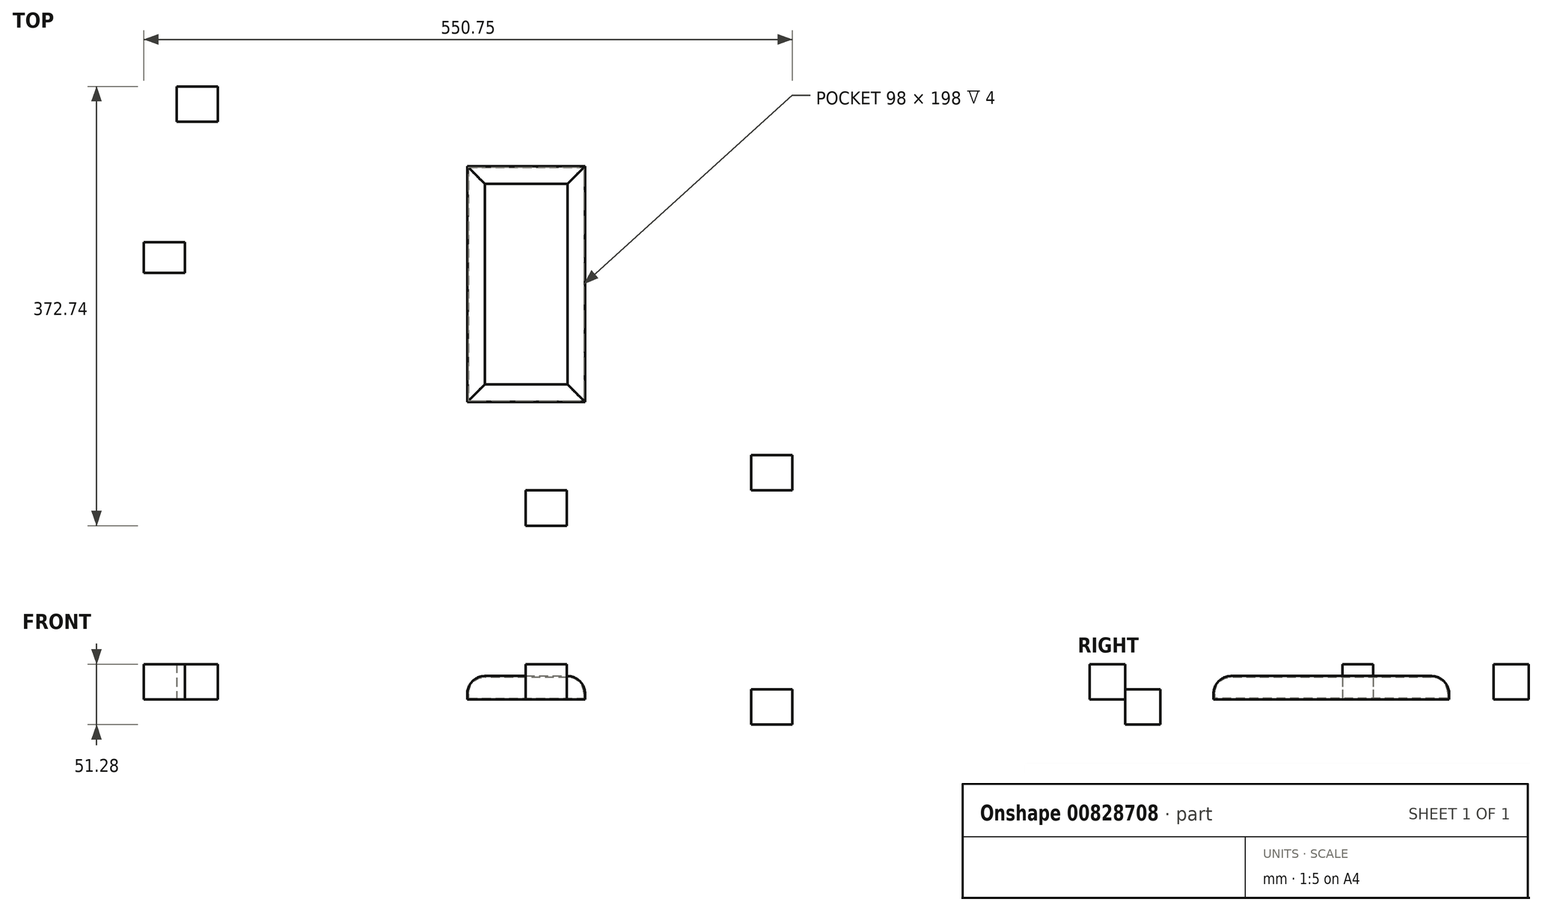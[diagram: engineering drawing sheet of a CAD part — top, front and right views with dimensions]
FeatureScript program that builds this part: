
annotation { "Feature Type Name" : "Feature", "Feature Type Description" : "" }
export const myFeature = defineFeature(function(context is Context, id is Id, definition is map)
    precondition{}
    {
        {
            var Q0;
            Q0=qCreatedBy(makeId("Top.planeOp"),FACE);
            var sketch = newSketch(context, id + "F0", { "sketchPlane" : qUnion([Q0])});
            skLineSegment(sketch, "E0.bottom", {"start": v(-289.22, 3.67) * mm, "end": v(-189.22, 3.67) * mm});
            skLineSegment(sketch, "E0.top", {"start": v(-289.22, -196.33) * mm, "end": v(-189.22, -196.33) * mm});
            skLineSegment(sketch, "E0.left", {"start": v(-289.22, 3.67) * mm, "end": v(-289.22, -196.33) * mm});
            skLineSegment(sketch, "E0.right", {"start": v(-189.22, 3.67) * mm, "end": v(-189.22, -196.33) * mm});
            skPoint(sketch, "E0.middle", {"position": v(-239.22, -96.33) * mm});
            skSolve(sketch);
        }
        {
            var Q0;
            Q0=makeQuery(id+"F0.imprint","IMPRINT",FACE,{"disambiguationData":[TD([[makeQuery(id+"F0.imprint","IMPRINT",EDGE,{"derivedFrom":sQuery(id+"F0.wireOp",EDGE,"E0.bottom")}),-1.0]])]});
            extrude(context, id + "F1", {"entities" : qUnion([Q0]), "depth" : 20 * mm, "offsetDistance" : 25 * mm});
        }
        {
            var Q0;
            Q0=makeQuery(id+"F1.opExtrude","CAP_EDGE",EDGE,{"disambiguationData":[OSD([sQuery(id+"F0.wireOp",EDGE,"E0.right")])],"isStart":false});
            var Q1;
            Q1=makeQuery(id+"F1.opExtrude","CAP_EDGE",EDGE,{"disambiguationData":[OSD([sQuery(id+"F0.wireOp",EDGE,"E0.top")])],"isStart":false});
            var Q2;
            Q2=makeQuery(id+"F1.opExtrude","CAP_EDGE",EDGE,{"disambiguationData":[OSD([sQuery(id+"F0.wireOp",EDGE,"E0.bottom")])],"isStart":false});
            var Q3;
            Q3=makeQuery(id+"F1.opExtrude","CAP_EDGE",EDGE,{"disambiguationData":[OSD([sQuery(id+"F0.wireOp",EDGE,"E0.left")])],"isStart":false});
            fillet(context, id + "F2", {"entities" : qUnion([Q0, Q1, Q2, Q3]), "radius" : 15 * mm, "tangentPropagation" : true, "allowEdgeOverflow" : false});
        }
        {
            var Q0;
            Q0=makeQuery(id+"F1.opExtrude","CAP_FACE",FACE,{"disambiguationData":[OSD([sQuery(id+"F0.wireOp",EDGE,"E0.bottom"),sQuery(id+"F0.wireOp",EDGE,"E0.top"),sQuery(id+"F0.wireOp",EDGE,"E0.left"),sQuery(id+"F0.wireOp",EDGE,"E0.right")])],"isStart":false});
            shell(context, id + "F3", {"entities" : qUnion([Q0]), "thickness" : 1 * mm});
        }
        {
            var Q0;
            Q0=qCreatedBy(makeId("Top.planeOp"),FACE);
            var sketch = newSketch(context, id + "F4", { "sketchPlane" : qUnion([Q0])});
            skLineSegment(sketch, "E1.bottom", {"start": v(-239.75, -271.36) * mm, "end": v(-204.75, -271.36) * mm});
            skLineSegment(sketch, "E1.top", {"start": v(-239.75, -301.36) * mm, "end": v(-204.75, -301.36) * mm});
            skLineSegment(sketch, "E1.left", {"start": v(-239.75, -271.36) * mm, "end": v(-239.75, -301.36) * mm});
            skLineSegment(sketch, "E1.right", {"start": v(-204.75, -271.36) * mm, "end": v(-204.75, -301.36) * mm});
            skSolve(sketch);
        }
        {
            var Q0;
            Q0 = qSketchRegion(id + "F4", true);
            extrude(context, id + "F5", {"entities" : qUnion([Q0]), "depth" : 30 * mm, "offsetDistance" : 25 * mm});
        }
        {
            var Q0;
            Q0=makeQuery(id+"F5.opExtrude","SWEPT_FACE",FACE,{"disambiguationData":[OSD([sQuery(id+"F4.wireOp",EDGE,"E1.bottom")])]});
            var sketch = newSketch(context, id + "F6", { "sketchPlane" : qUnion([Q0])});
            skLineSegment(sketch, "E2.bottom", {"start": v(48.2, 8.72) * mm, "end": v(13.2, 8.72) * mm});
            skLineSegment(sketch, "E2.top", {"start": v(48.2, -21.28) * mm, "end": v(13.2, -21.28) * mm});
            skLineSegment(sketch, "E2.left", {"start": v(48.2, 8.72) * mm, "end": v(48.2, -21.28) * mm});
            skLineSegment(sketch, "E2.right", {"start": v(13.2, 8.72) * mm, "end": v(13.2, -21.28) * mm});
            skSolve(sketch);
        }
        {
            var Q0;
            Q0 = qSketchRegion(id + "F6", true);
            extrude(context, id + "F7", {"entities" : qUnion([Q0]), "depth" : 30 * mm, "offsetDistance" : 25 * mm});
        }
        {
            var Q0;
            Q0=qCreatedBy(makeId("Top.planeOp"),FACE);
            var sketch = newSketch(context, id + "F8", { "sketchPlane" : qUnion([Q0])});
            skLineSegment(sketch, "E3.bottom", {"start": v(-563.95, -60.89) * mm, "end": v(-528.95, -60.89) * mm});
            skLineSegment(sketch, "E3.top", {"start": v(-563.95, -86.75) * mm, "end": v(-528.95, -86.75) * mm});
            skLineSegment(sketch, "E3.left", {"start": v(-563.95, -60.89) * mm, "end": v(-563.95, -86.75) * mm});
            skLineSegment(sketch, "E3.right", {"start": v(-528.95, -60.89) * mm, "end": v(-528.95, -86.75) * mm});
            skSolve(sketch);
        }
        {
            var Q0;
            Q0 = qSketchRegion(id + "F8", true);
            extrude(context, id + "F9", {"entities" : qUnion([Q0]), "depth" : 30 * mm, "offsetDistance" : 25 * mm});
        }
        {
            var Q0;
            Q0=qCreatedBy(makeId("Top.planeOp"),FACE);
            var sketch = newSketch(context, id + "F10", { "sketchPlane" : qUnion([Q0])});
            skLineSegment(sketch, "E4.bottom", {"start": v(-535.9, 71.38) * mm, "end": v(-500.9, 71.38) * mm});
            skLineSegment(sketch, "E4.top", {"start": v(-535.9, 41.38) * mm, "end": v(-500.9, 41.38) * mm});
            skLineSegment(sketch, "E4.left", {"start": v(-535.9, 71.38) * mm, "end": v(-535.9, 41.38) * mm});
            skLineSegment(sketch, "E4.right", {"start": v(-500.9, 71.38) * mm, "end": v(-500.9, 41.38) * mm});
            skSolve(sketch);
        }
        {
            var Q0;
            Q0 = qSketchRegion(id + "F10", true);
            extrude(context, id + "F11", {"entities" : qUnion([Q0]), "depth" : 30 * mm, "offsetDistance" : 25 * mm});
        }
    });
